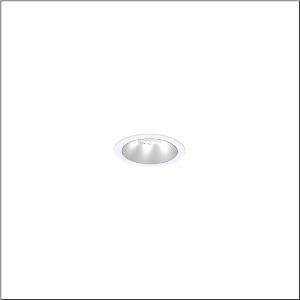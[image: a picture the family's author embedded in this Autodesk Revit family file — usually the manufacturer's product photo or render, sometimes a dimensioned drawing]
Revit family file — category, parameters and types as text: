
# Revit family: lunis_21_s_51db19ta91c
name_source: partatom
category: Lighting Fixtures
units: mm (PartAtom-declared; Revit-internal decimal feet)

## family parameters
Cut with Voids When Loaded = No
Host = Face
Light Source = No
Part Type = Normal
Room Calculation Point = No
Round Connector Dimension = Use Diameter
Shared = No

## types (1)
- --- (1 x LED, 1210 lm, 8 W, 4000K)
    Apparent Load = 8 VA
    CIE Flux Codes = 95 100 100 100 100
    Color Rendering = 80
    Color Temperature = 4000K
    Default Elevation = 1800 mm
    Description = Lunis 21,  S, downlight, light control with lens, of PMMA, anti glare with reflector, of plastic, matt, light emission: direct distribution, LED rated luminous flux: 910lm, light colour: 8tw, with terminal, 5-pole, mains connection: 220..240V, AC, 50..60Hz, housing, round, of diecast aluminium, traffic white (RAL 9016), diameter: 84mm, clamping range: 1..40mm, protection rating (complete): IP20, protection rating (on room side): IP54, insulation class (complete): insulation class II (safety insulation), certification: CE, impact resistance: IK03, packaging unit: 1 piece
    Height = 0 mm  [stored 0 ft]
    Lamp = 1 x LED
    Lamp Light Flux = 1210 lm
    Lamp Power = 8 W
    Lamp count = 1
    Length = 84 mm
    Luminous efficacy = 151 lm/W
    Manufacturer = Siteco
    ModVariant = No
    Model = 51DB19TA91C
    Mounting Place = Ceiling
    Mounting Type = Recessed
    Number of Poles = 1
    OnlyDefault = Yes
    Power Factor = 1
    Product Name = Lunis 21 S
    Product group = downlight
    ProductGroupID = 400
    Protection Class = Protection class II
    Protection Degree = IP 20
    RLX_Detail_Level = 1
    RLX_Emergency_Light_Flux = 0 lm
    RLX_Emergency_Type = 0
    RLX_Emergency_Type_DB = No
    RlxData = <blob elided: 8641 chars, md5=7574234a>
    Socket = socket
    Standby Power = 0 W
    System Light Flux = 1210 lm
    System Power = 8 W
    Type Comments = individual setting: colour temperature 4000K, luminous flux: 100 % | (OFF | OFF | ON | OFF) | 200 mA
    Type Image = l_1290846.jpg
    URL = http://relux.com
    VarID = @adj_001093
    Voltage = 0 V
    Weight = 0.00 kg
    Width = 0 mm  [stored 0 ft]

note: [stored X ft] marks values corroborated as IEEE doubles in the binary element streams (Revit-internal decimal feet)

## geometry (parser evidence)
native form markers: Sweep x9
no freeform markers — native parametric forms only
